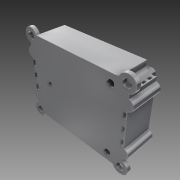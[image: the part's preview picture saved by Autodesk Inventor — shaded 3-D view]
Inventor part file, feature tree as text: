
AUTODESK INVENTOR PART (.ipt)
format: ipt  version: 2014 (Build 180170000, 170)  size: 958,976 bytes
history: native  units: mm
features: extrude x17, sketch x10, fillet x5, mirror x5, projected_geometry x3, plane x1, pattern_circular x1, revolve x1, chamfer x1
ambient origin geometry x8: Origin, YZ Plane, XZ Plane, XY Plane, X Axis, Y Axis, Z Axis, Center Point
bodies: Solid1 (feature_tree)
feature tree (44):
  extrude  "Base"  Depth=6.0mm
  extrude  "Floor & Servo Walls"  Depth=3.0mm
  plane  "Work Plane2"
  extrude  "Framing"  Depth=3.0mm
  fillet  "Fillet2"  Radius=150.0mm
  extrude  "Potentiometer Housing"  Depth=71.0mm
  extrude  "Centre Nail Mount"  Depth=30.0mm
  extrude  "Extrusion7"  Depth=35.0mm TaperAngle=0.0deg
  pattern_circular  "Circular Pattern1"  [2 undecoded]
  revolve  "Revolution1"  [1 undecoded]
  fillet  "Fillet5"  Radius=12.0mm
  fillet  "Fillet6"  Radius=12.0mm
  fillet  "Fillet7"  Radius=12.0mm
  fillet  "Fillet4"  Radius=24.0mm
  extrude  "Extrusion8"  Depth=3.0mm
  sketch  "Sketch8"  dims[d22=10.0mm d23=10.0mm d25=71.0mm]
  extrude  "Extrusion9"  Depth=3.0mm
  extrude  "Extrusion10"  Depth=3.0mm
  mirror  "Mirror1"
  mirror  "Mirror2"
  chamfer  "Chamfer1"  Distance=10.0mm
  sketch  "Sketch10"  dims[d26=30.0mm d27=54.5mm d28=54.5mm]
  extrude  "Extrusion12"  Depth=24.0mm
  extrude  "Extrusion13"  Depth=4.0mm
  extrude  "Extrusion14"  Depth=69.0mm
  mirror  "Mirror3"
  extrude  "Extrusion15"  Depth=69.0mm
  extrude  "Extrusion16"  Depth=2.0mm
  extrude  "Extrusion17"  Depth=2.0mm
  mirror  "Mirror4"
  extrude  "Extrusion18"  Depth=2.0mm
  extrude  "Extrusion19"  Depth=2.0mm
  mirror  "Mirror5"
  sketch  "Sketch3"  dims[d1=6.0mm d2=6.0mm d3=6.0mm]
  sketch  "Sketch5"  dims[d4=6.0mm d5=3.0mm]
  sketch  "Sketch7"  dims[d6=3.0mm d7=3.0mm d16=150.0mm d17=70.0mm]
  projected_geometry  "Projected Loop2"
  sketch  "Sketch11"  dims[d29=5.0mm d30=0.0mm d31=35.0mm d32=0.0mm]
  sketch  "Sketch12"  dims[d35=14.0mm]
  sketch  "Sketch13"  dims[d36=3.0mm]
  sketch  "Sketch14"  dims[d37=3.0mm]
  projected_geometry  "Projected Loop3"
  projected_geometry  "Projected Loop4"
  sketch  "Sketch15"  dims[d38=3.0mm d39=3.0mm d45=12.0mm d46=12.0mm d47=12.0mm d48=12.0mm d49=24.0mm d51=3.0mm d52=3.0mm d53=3.0mm d54=10.0mm d55=0.0mm d67=24.0mm d69=4.0mm d75=9.55mm d76=9.55mm d79=2.0mm d80=2.0mm d81=2.0mm d82=2.0mm d83=12.0mm d84=0.0mm d85=11.0mm d86=2.0mm d87=3.0mm d88=3.0mm d89=3.0mm d90=3.0mm d91=2.0mm d92=0.0mm d97=40.0mm d98=0.0mm d99=40.0mm d100=360.0deg d103=1.5mm d104=6.0mm d105=35.0mm d106=10.0mm d107=90.0deg d108=2.0mm d109=2.0mm d111=4.0mm d112=10.0mm d113=1.0mm d114=2.0mm d115=10.0mm d116=20.0mm d118=10.0mm d119=20.0mm d120=10.0mm d121=20.0mm d122=10.0mm d123=20.374355mm d125=30.0mm d126=30.0mm d127=30.0mm d128=30.0mm d131=6.0mm d132=6.0mm d133=6.0mm d134=6.0mm d135=10.0mm d136=10.0mm d137=3.0mm d139=3.0mm d140=3.0mm d141=3.0mm d142=3.0mm d143=3.0mm d144=3.0mm d145=3.0mm d146=140.0mm d147=3.0mm d148=6.35mm d149=4.0mm d150=8.726646mm d151=8.726646mm d152=2.0mm d153=2.0mm d154=2.0mm d155=2.0mm d156=1.0mm d157=2.0mm d158=2.0mm d159=35.0mm d160=4.775mm d161=4.775mm d171=5.0mm d172=0.0mm d173=3.38105mm d174=3.38105mm d175=6.0mm d176=4.1656mm d177=5.0mm d178=30.0mm d181=40.0mm d182=0.0mm d183=20.0mm d184=0.0mm d187=1.0mm d188=5.0mm d189=2.0mm d190=45.0deg d191=8.2804mm d192=6.1989mm d193=6.1989mm d196=5.207mm d197=5.207mm d200=12.3952mm d201=1.328045mm d202=1.328045mm d203=1.328045mm d204=1.328045mm d205=4.1402mm d206=4.1402mm d207=7.4434mm d208=0.0mm d210=15.0mm d211=0.0mm d212=40.0mm d213=0.0mm d214=80.0mm d215=0.0mm d216=8.509mm d221=5.334mm d222=3.0mm d223=0.0mm d224=15.0mm d226=15.0mm d227=18.0mm d228=5.0mm d229=8.509mm d230=5.0mm d231=0.0mm d232=6.35mm d233=1.6mm d234=1.6mm d235=1.6mm d236=1.6mm d237=5.0mm d238=0.0mm d239=5.0mm d240=5.0mm d241=5.0mm d242=5.0mm d243=4.0mm d244=4.0mm d245=4.0mm d246=4.0mm d247=4.0mm d248=1.5mm d249=1.5mm d250=3.0mm d251=90.0mm d252=0.0mm d253=8.0mm d254=3.0mm d255=1.5mm d256=1.5mm d257=16.0mm d258=8.0mm d259=8.0mm d260=16.0mm d261=4.0mm d262=90.0mm d263=0.0mm d264=69.0mm]
note: 3 required parameter values undecoded (feature->parameter linkage not recoverable at this tier; creation-order binding heuristic only, values carry confidence <= 0.55)